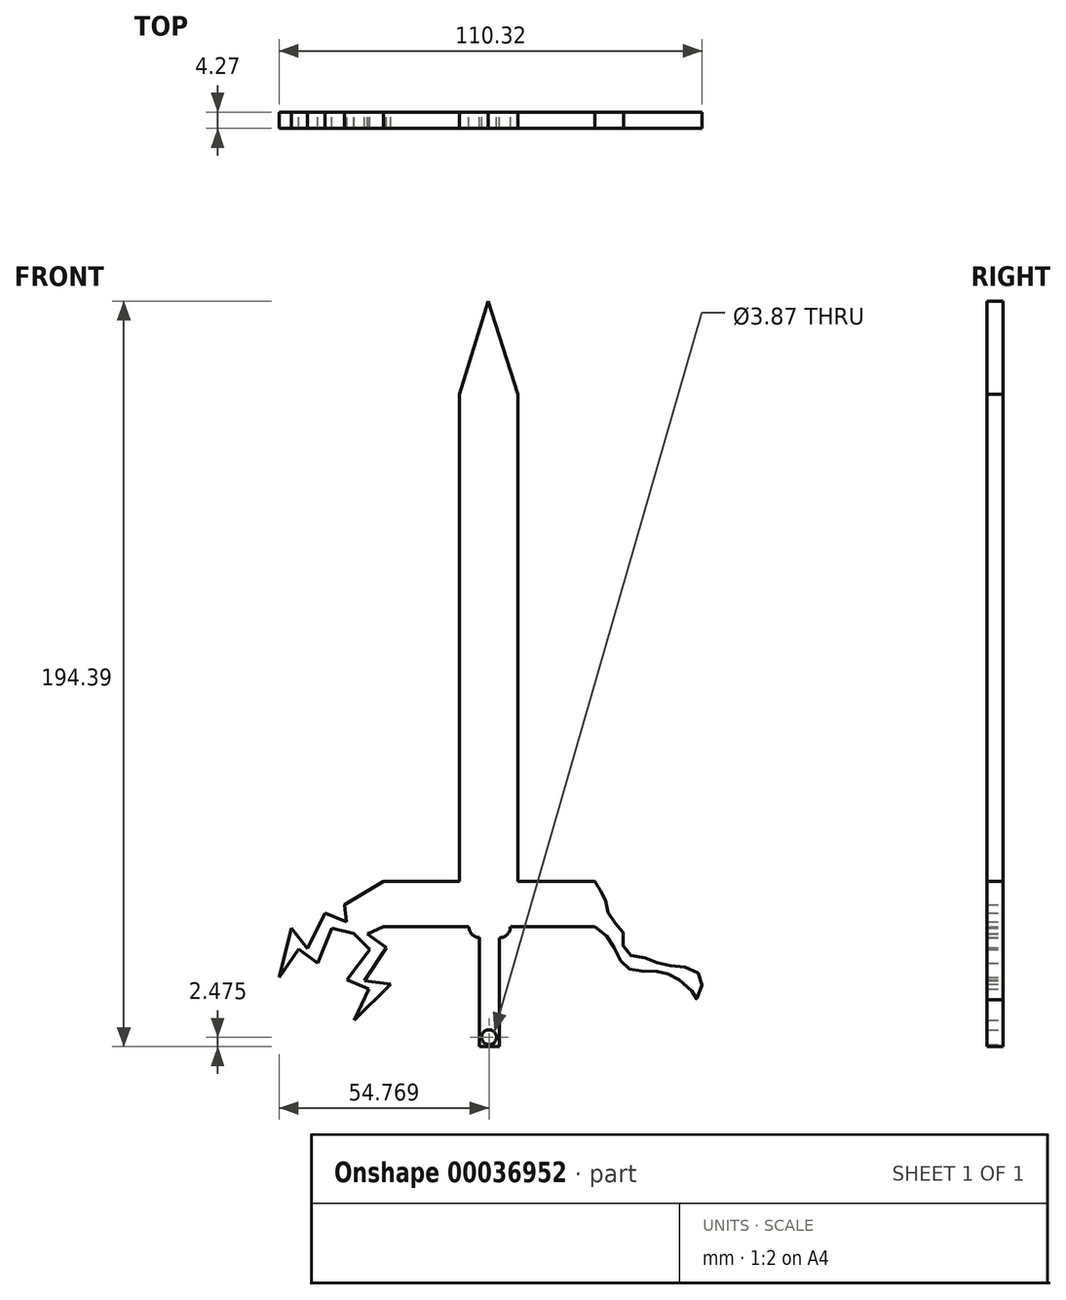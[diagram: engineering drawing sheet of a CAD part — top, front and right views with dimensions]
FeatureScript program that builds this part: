
annotation { "Feature Type Name" : "Feature", "Feature Type Description" : "" }
export const myFeature = defineFeature(function(context is Context, id is Id, definition is map)
    precondition{}
    {
        {
            var Q0;
            Q0=qCreatedBy(makeId("Front.planeOp"),FACE);
            var sketch = newSketch(context, id + "F0", { "sketchPlane" : qUnion([Q0])});
            skLineSegment(sketch, "E0.top", {"start": v(-10.35, -26.73) * mm, "end": v(4.9, -26.73) * mm});
            skLineSegment(sketch, "E0.left", {"start": v(-10.35, 100.27) * mm, "end": v(-10.35, -26.73) * mm});
            skLineSegment(sketch, "E0.right", {"start": v(4.9, 100.27) * mm, "end": v(4.9, -26.73) * mm});
            skLineSegment(sketch, "E1.bottom", {"start": v(-30.2, -26.73) * mm, "end": v(24.93, -26.73) * mm});
            skLineSegment(sketch, "E1.top", {"start": v(-30.2, -38.52) * mm, "end": v(-7.95, -38.52) * mm});
            skLineSegment(sketch, "E2.top", {"start": v(-5.2, -69.82) * mm, "end": v(0, -69.82) * mm});
            skLineSegment(sketch, "E2.right", {"start": v(0, -41.43) * mm, "end": v(0, -69.82) * mm});
            skLineSegment(sketch, "E3", {"start": v(-10.35, 100.27) * mm, "end": v(-2.9, 124.57) * mm});
            skLineSegment(sketch, "E4", {"start": v(-2.9, 124.57) * mm, "end": v(4.9, 100.27) * mm});
            skLineSegment(sketch, "E5", {"start": v(-37.88, -40.25) * mm, "end": v(-33.74, -44.52) * mm});
            skLineSegment(sketch, "E6", {"start": v(-33.74, -44.52) * mm, "end": v(-39.76, -52.42) * mm});
            skLineSegment(sketch, "E7", {"start": v(-39.76, -52.42) * mm, "end": v(-33.99, -54.8) * mm});
            skLineSegment(sketch, "E8", {"start": v(-33.99, -54.8) * mm, "end": v(-37.75, -62.95) * mm});
            skLineSegment(sketch, "E9", {"start": v(-37.75, -62.95) * mm, "end": v(-28.35, -53.55) * mm});
            skLineSegment(sketch, "E10", {"start": v(-28.35, -53.55) * mm, "end": v(-35.12, -52.67) * mm});
            skLineSegment(sketch, "E11", {"start": v(-35.12, -52.67) * mm, "end": v(-29.47, -44.02) * mm});
            skLineSegment(sketch, "E12", {"start": v(-29.47, -44.02) * mm, "end": v(-34.37, -40.38) * mm});
            skLineSegment(sketch, "E13", {"start": v(-34.37, -40.38) * mm, "end": v(-30.2, -38.52) * mm});
            skLineSegment(sketch, "E14.MirrorCS", {"start": v(-30.2, -26.73) * mm, "end": v(-40.33, -32.78) * mm});
            skLineSegment(sketch, "E15.MirrorCS", {"start": v(-39.79, -37.3) * mm, "end": v(-40.33, -32.78) * mm});
            skLineSegment(sketch, "E16.MirrorCS", {"start": v(-45.42, -34.97) * mm, "end": v(-39.79, -37.3) * mm});
            skLineSegment(sketch, "E17.MirrorCS", {"start": v(-49.95, -44.25) * mm, "end": v(-45.42, -34.97) * mm});
            skLineSegment(sketch, "E18.MirrorCS", {"start": v(-37.88, -40.25) * mm, "end": v(-43.66, -38.89) * mm});
            skLineSegment(sketch, "E19.MirrorCS", {"start": v(-43.66, -38.89) * mm, "end": v(-47.35, -48.1) * mm});
            skLineSegment(sketch, "E20.MirrorCS", {"start": v(-54.18, -38.89) * mm, "end": v(-49.95, -44.25) * mm});
            skLineSegment(sketch, "E21.MirrorCS", {"start": v(-47.35, -48.1) * mm, "end": v(-52.36, -44.38) * mm});
            skLineSegment(sketch, "E22.MirrorCS", {"start": v(-57.43, -51.79) * mm, "end": v(-54.18, -38.89) * mm});
            skLineSegment(sketch, "E23.MirrorCS", {"start": v(-52.36, -44.38) * mm, "end": v(-57.43, -51.79) * mm});
            skFitSpline(sketch, "E24", {"points": [v(24.93, -38.52) * mm, v(28.17, -41.08) * mm, v(30, -44.18) * mm, v(31.97, -47.84) * mm, v(33.94, -49.53) * mm, v(36.62, -50.1) * mm, v(41.12, -50.23) * mm, v(43.66, -50.65) * mm, v(45.63, -51.78) * mm, v(49.85, -54.6) * mm, v(51.12, -57.55) * mm, v(52.52, -55.16) * mm, v(52.52, -51.5) * mm, v(49.7, -49.39) * mm, v(45.77, -48.68) * mm, v(41.83, -48.26) * mm, v(39.15, -46.85) * mm, v(35.2, -46.3) * mm, v(32.54, -44.46) * mm, v(32.4, -41.22) * mm, v(31.4, -38.52) * mm, v(29.02, -36.58) * mm, v(28.03, -33.2) * mm, v(27.6, -31.23) * mm, v(26.48, -29.26) * mm, v(24.93, -26.73) * mm], "startDerivative": vector(79.9, -53.42) * mm, "endDerivative": vector(-41.21, 68.31) * mm});
            skFitSpline(sketch, "E25", {"points": [v(26.48, -29.26) * mm, v(29.2, -31.12) * mm, v(31.21, -34.79) * mm, v(33.22, -38.52) * mm, v(33.81, -40.82) * mm, v(35, -43.66) * mm, v(37.72, -45.08) * mm, v(39.97, -45.8) * mm, v(43.05, -47.21) * mm, v(45.18, -47.45) * mm, v(48.85, -47.57) * mm, v(54.4, -48.04) * mm, v(57.72, -47.45) * mm, v(54.4, -46.39) * mm, v(49.91, -46.27) * mm, v(45.06, -44.02) * mm, v(42.45, -41.18) * mm, v(39.14, -41.06) * mm, v(36.54, -38.52) * mm, v(36.18, -34.67) * mm, v(34.4, -33.37) * mm, v(31.4, -29.26) * mm, v(24.93, -26.73) * mm], "startDerivative": vector(69.24, -35.48) * mm, "endDerivative": vector(-118.31, 25.26) * mm});
            skFitSpline(sketch, "E26", {"points": [v(34.4, -33.37) * mm, v(38.13, -34.69) * mm, v(39.81, -37.6) * mm, v(41.49, -39.16) * mm, v(44.95, -40.5) * mm, v(48.41, -42.73) * mm, v(51.65, -44.86) * mm, v(57.13, -45.2) * mm, v(55.45, -43.63) * mm, v(50.87, -41.62) * mm, v(47.97, -39.6) * mm, v(46.51, -36.14) * mm, v(41.82, -34.8) * mm, v(39.14, -33.37) * mm, v(37.69, -30.22) * mm, v(34.4, -29.44) * mm, v(32.66, -27.87) * mm, v(29.98, -26.31) * mm, v(24.93, -26.73) * mm], "startDerivative": vector(73.72, -12.75) * mm, "endDerivative": vector(-82.7, -16.33) * mm});
            skArc(sketch, "E27", {"start": v(-7.95, -38.52) * mm, "mid": v(-7.15, -40.5) * mm, "end": v(-5.2, -41.37) * mm});
            skArc(sketch, "E28.trimOffspring", {"start": v(0, -41.43) * mm, "mid": v(2.05, -40.58) * mm, "end": v(2.9, -38.52) * mm});
            skLineSegment(sketch, "E29.trimOffspring", {"start": v(-5.2, -41.37) * mm, "end": v(-5.2, -69.82) * mm});
            skLineSegment(sketch, "E30.trimOffspring", {"start": v(2.9, -38.52) * mm, "end": v(24.93, -38.52) * mm});
            skLineSegment(sketch, "E31", {"start": v(-5.2, -41.37) * mm, "end": v(0, -41.43) * mm});
            skLineSegment(sketch, "E32.trimOffspring", {"start": v(0, -38.52) * mm, "end": v(2.9, -38.52) * mm});
            skLineSegment(sketch, "E33", {"start": v(-7.95, -38.52) * mm, "end": v(-5.1, -38.52) * mm});
            skCircle(sketch, "E34", {"center": v(-2.66, -67.34) * mm, "radius": 1.94 * mm});
            skSolve(sketch);
        }
        {
            var Q0;
            {var subQ2=sQuery(id+"F0.wireOp",EDGE,"E0.left");Q0=makeQuery(id+"F0.imprint","IMPRINT",FACE,{"disambiguationData":[TD([[makeQuery(id+"F0.imprint","IMPRINT",EDGE,{"derivedFrom":subQ2}),1.0]])]});}
            var Q1;
            Q1=makeQuery(id+"F0.imprint","IMPRINT",FACE,{"disambiguationData":[TD([[makeQuery(id+"F0.imprint","IMPRINT",EDGE,{"derivedFrom":sQuery(id+"F0.wireOp",EDGE,"E2.bottom")}),-1.0]])]});
            var Q2;
            {var subQ2=sQuery(id+"F0.wireOp",EDGE,"E1.left");Q2=makeQuery(id+"F0.imprint","IMPRINT",FACE,{"disambiguationData":[TD([[makeQuery(id+"F0.imprint","IMPRINT",EDGE,{"derivedFrom":subQ2}),1.0]])]});}
            extrude(context, id + "F1", {"entities" : qUnion([Q0, Q1, Q2]), "depth" : 4.26 * mm});
        }
        {
            var Q0;
            {var subQ4=sQuery(id+"F0.wireOp",EDGE,"E1.top");Q0=makeQuery(id+"F0.imprint","IMPRINT",FACE,{"disambiguationData":[TD([[makeQuery(id+"F0.imprint","IMPRINT",EDGE,{"derivedFrom":subQ4}),1.0]])]});}
            var Q1;
            Q1=makeQuery(id+"F0.imprint","IMPRINT",FACE,{"disambiguationData":[TD([[makeQuery(id+"F0.imprint","IMPRINT",EDGE,{"derivedFrom":sQuery(id+"F0.wireOp",EDGE,"E2.top")}),1.0]])]});
            var Q2;
            {var subQ3=sQuery(id+"F0.wireOp",EDGE,"E2.left");Q2=makeQuery(id+"F0.imprint","IMPRINT",FACE,{"disambiguationData":[TD([[makeQuery(id+"F0.imprint","IMPRINT",EDGE,{"derivedFrom":subQ3}),-1.0]])]});}
            extrude(context, id + "F2", {"entities" : qUnion([Q0, Q1, Q2]), "operationType" : NewBodyOperationType.ADD, "depth" : 4.27 * mm});
        }
    });
